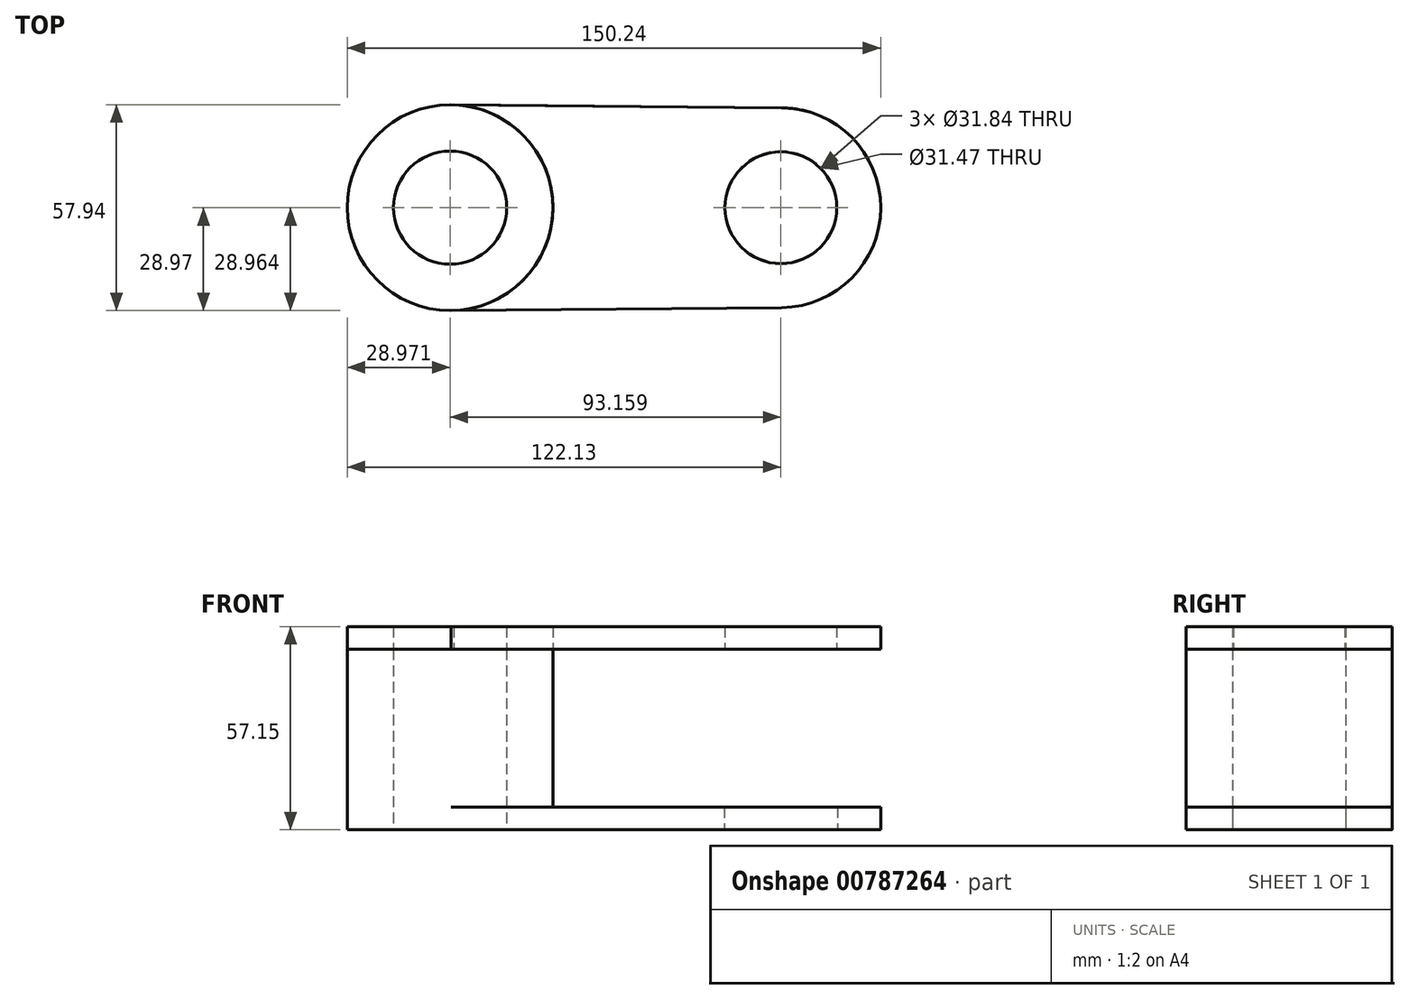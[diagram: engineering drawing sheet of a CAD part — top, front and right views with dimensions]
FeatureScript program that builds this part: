
annotation { "Feature Type Name" : "Feature", "Feature Type Description" : "" }
export const myFeature = defineFeature(function(context is Context, id is Id, definition is map)
    precondition{}
    {
        {
            var Q0;
            Q0=qCreatedBy(makeId("Top.planeOp"),FACE);
            var sketch = newSketch(context, id + "F0", { "sketchPlane" : qUnion([Q0])});
            skCircle(sketch, "E0", {"center": v(-46.58, 0) * mm, "radius": 15.92 * mm});
            skCircle(sketch, "E1", {"center": v(46.58, 0) * mm, "radius": 15.92 * mm});
            skArc(sketch, "E2", {"start": v(-46.3, 28.97) * mm, "mid": v(-75.55, 0) * mm, "end": v(-46.3, -28.97) * mm});
            skArc(sketch, "E3", {"start": v(46.84, -28.1) * mm, "mid": v(74.68, 0) * mm, "end": v(46.84, 28.1) * mm});
            skLineSegment(sketch, "E4", {"start": v(-46.3, 28.97) * mm, "end": v(46.84, 28.1) * mm});
            skLineSegment(sketch, "E5", {"start": v(46.84, -28.1) * mm, "end": v(-46.3, -28.97) * mm});
            skArc(sketch, "E6", {"start": v(-46.3, -28.97) * mm, "mid": v(-17.6, 0) * mm, "end": v(-46.3, 28.97) * mm});
            skSolve(sketch);
        }
        {
            var Q0;
            Q0=makeQuery(id+"F0.imprint","IMPRINT",FACE,{"disambiguationData":[TD([[makeQuery(id+"F0.imprint","IMPRINT",EDGE,{"derivedFrom":sQuery(id+"F0.wireOp",EDGE,"E0")}),-1.0]])]});
            extrude(context, id + "F1", {"entities" : qUnion([Q0]), "depth" : 50.8 * mm, "offsetDistance" : 25.4 * mm});
        }
        {
            var Q0;
            Q0=makeQuery(id+"F0.imprint","IMPRINT",FACE,{"disambiguationData":[TD([[makeQuery(id+"F0.imprint","IMPRINT",EDGE,{"derivedFrom":sQuery(id+"F0.wireOp",EDGE,"E1")}),-1.0]])]});
            extrude(context, id + "F2", {"entities" : qUnion([Q0]), "operationType" : NewBodyOperationType.ADD, "depth" : 6.35 * mm, "offsetDistance" : 25.4 * mm});
        }
        {
            var Q0;
            Q0=makeQuery(id+"F1.opExtrude","CAP_FACE",FACE,{"disambiguationData":[OSD([sQuery(id+"F0.wireOp",EDGE,"E0"),sQuery(id+"F0.wireOp",EDGE,"E2"),sQuery(id+"F0.wireOp",EDGE,"E6")])],"isStart":false});
            var sketch = newSketch(context, id + "F3", { "sketchPlane" : qUnion([Q0])});
            skLineSegment(sketch, "E7", {"start": v(-47.1, 28.97) * mm, "end": v(46.83, 28.1) * mm});
            skLineSegment(sketch, "E8", {"start": v(-46.3, -28.97) * mm, "end": v(46.84, -28.11) * mm});
            skArc(sketch, "E9", {"start": v(46.84, -28.11) * mm, "mid": v(74.69, 0) * mm, "end": v(46.83, 28.1) * mm});
            skCircle(sketch, "E10", {"center": v(46.58, 0) * mm, "radius": 15.74 * mm});
            skSolve(sketch);
        }
        {
            var Q0;
            {var subQ1=sQuery(id+"F3.wireOp",EDGE,"E8");Q0=makeQuery(id+"F3.imprint","IMPRINT",FACE,{"disambiguationData":[TD([[makeQuery(id+"F3.imprint","IMPRINT",EDGE,{"derivedFrom":subQ1}),1.0]])]});}
            extrude(context, id + "F4", {"entities" : qUnion([Q0]), "depth" : 6.35 * mm, "offsetDistance" : 25.4 * mm});
        }
        {
            var Q0;
            Q0=makeQuery(id+"F1.opExtrude","CAP_FACE",FACE,{"disambiguationData":[OSD([sQuery(id+"F0.wireOp",EDGE,"E0"),sQuery(id+"F0.wireOp",EDGE,"E2"),sQuery(id+"F0.wireOp",EDGE,"E6")])],"isStart":false});
            extrude(context, id + "F5", {"entities" : qUnion([Q0]), "depth" : 6.35 * mm, "offsetDistance" : 25.4 * mm});
        }
    });
